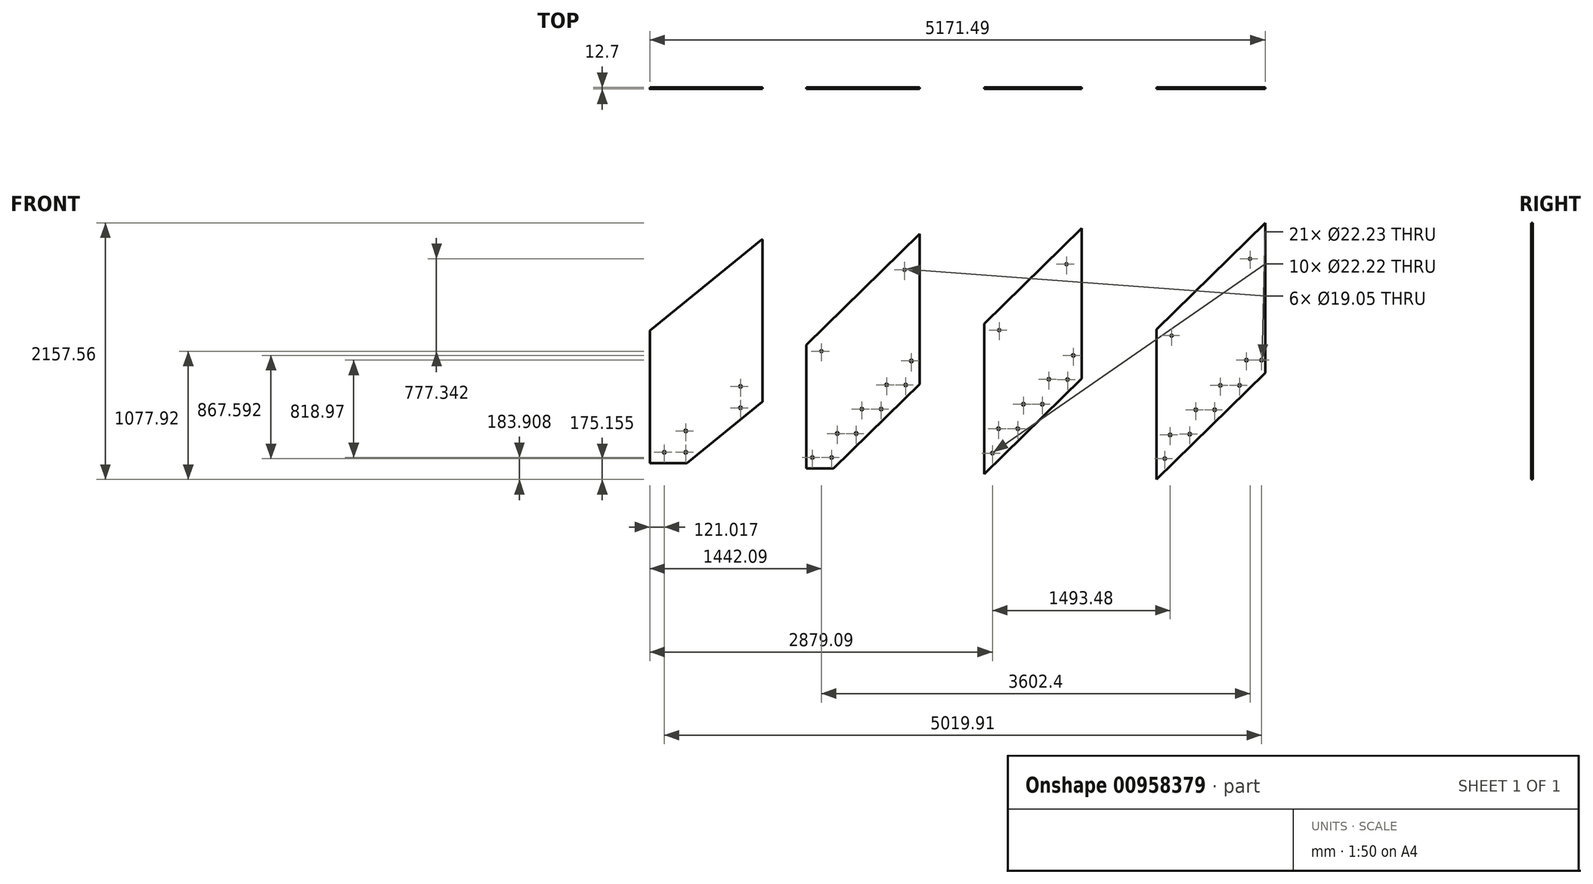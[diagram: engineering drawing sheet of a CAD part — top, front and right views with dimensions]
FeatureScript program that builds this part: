
annotation { "Feature Type Name" : "Feature", "Feature Type Description" : "" }
export const myFeature = defineFeature(function(context is Context, id is Id, definition is map)
    precondition{}
    {
        {
            var Q0;
            Q0=qCreatedBy(makeId("Front.planeOp"),FACE);
            var sketch = newSketch(context, id + "F0", { "sketchPlane" : qUnion([Q0])});
            skLineSegment(sketch, "E0", {"start": v(473.07, -425.21) * mm, "end": v(473.07, 941.15) * mm});
            skLineSegment(sketch, "E1", {"start": v(-161.93, -941.15) * mm, "end": v(-473.08, -941.15) * mm});
            skLineSegment(sketch, "E2", {"start": v(-161.93, -941.15) * mm, "end": v(473.08, -425.21) * mm});
            skLineSegment(sketch, "E3", {"start": v(-473.08, -941.15) * mm, "end": v(-473.08, 172.4) * mm});
            skLineSegment(sketch, "E4", {"start": v(-473.08, 172.4) * mm, "end": v(473.08, 941.15) * mm});
            skCircle(sketch, "E5", {"center": v(-171.45, -670.7) * mm, "radius": 11.11 * mm});
            skCircle(sketch, "E6", {"center": v(-171.45, -850.7) * mm, "radius": 11.11 * mm});
            skCircle(sketch, "E7", {"center": v(288.93, -296.65) * mm, "radius": 11.11 * mm});
            skCircle(sketch, "E8", {"center": v(288.93, -476.65) * mm, "radius": 11.11 * mm});
            skCircle(sketch, "E9", {"center": v(-352.06, -850.7) * mm, "radius": 11.11 * mm});
            skSolve(sketch);
        }
        {
            var Q0;
            Q0=makeQuery(id+"F0.imprint","IMPRINT",FACE,{"disambiguationData":[TD([[makeQuery(id+"F0.imprint","IMPRINT",EDGE,{"derivedFrom":sQuery(id+"F0.wireOp",EDGE,"E0")}),1.0]])]});
            extrude(context, id + "F1", {"entities" : qUnion([Q0]), "depth" : 12.7 * mm, "offsetDistance" : 25.4 * mm});
        }
        {
            var Q0;
            Q0=makeQuery(id+"F1.opExtrude","SWEPT_EDGE",EDGE,{"disambiguationData":[OSD([sQuery(id+"F0.wireOp",EDGE,"E0"),sQuery(id+"F0.wireOp",EDGE,"E4")])]});
            var Q1;
            Q1=makeQuery(id+"F1.opExtrude","SWEPT_EDGE",EDGE,{"disambiguationData":[OSD([sQuery(id+"F0.wireOp",EDGE,"E3"),sQuery(id+"F0.wireOp",EDGE,"E4")])]});
            var Q2;
            Q2=makeQuery(id+"F1.opExtrude","SWEPT_EDGE",EDGE,{"disambiguationData":[OSD([sQuery(id+"F0.wireOp",EDGE,"E1"),sQuery(id+"F0.wireOp",EDGE,"E3")])]});
            var Q3;
            Q3=makeQuery(id+"F1.opExtrude","SWEPT_EDGE",EDGE,{"disambiguationData":[OSD([sQuery(id+"F0.wireOp",EDGE,"E1"),sQuery(id+"F0.wireOp",EDGE,"E2")])]});
            var Q4;
            Q4=makeQuery(id+"F1.opExtrude","SWEPT_EDGE",EDGE,{"disambiguationData":[OSD([sQuery(id+"F0.wireOp",EDGE,"E0"),sQuery(id+"F0.wireOp",EDGE,"E2")])]});
            fillet(context, id + "F2", {"entities" : qUnion([Q0, Q1, Q2, Q3, Q4]), "radius" : 3.17 * mm, "tangentPropagation" : true, "allowEdgeOverflow" : false});
        }
        {
            var Q0;
            Q0=qCreatedBy(makeId("Front.planeOp"),FACE);
            var sketch = newSketch(context, id + "F3", { "sketchPlane" : qUnion([Q0])});
            skLineSegment(sketch, "E10", {"start": v(1661.16, -407.23) * mm, "end": v(1070.61, -986) * mm});
            skLineSegment(sketch, "E11", {"start": v(1794.51, 986) * mm, "end": v(842.01, 52.5) * mm});
            skLineSegment(sketch, "E12", {"start": v(842.01, -986) * mm, "end": v(842.01, 52.5) * mm});
            skCircle(sketch, "E13", {"center": v(892.81, -894.87) * mm, "radius": 11.11 * mm});
            skCircle(sketch, "E14", {"center": v(1054.74, -894.87) * mm, "radius": 11.11 * mm});
            skCircle(sketch, "E15", {"center": v(1261.11, -692.61) * mm, "radius": 11.11 * mm});
            skCircle(sketch, "E16", {"center": v(1470.82, -487.08) * mm, "radius": 11.11 * mm});
            skCircle(sketch, "E17", {"center": v(1308.74, -487.08) * mm, "radius": 11.11 * mm});
            skCircle(sketch, "E18", {"center": v(1516.74, -283.37) * mm, "radius": 11.11 * mm});
            skCircle(sketch, "E19", {"center": v(969.01, -0.86) * mm, "radius": 9.53 * mm});
            skLineSegment(sketch, "E20", {"start": v(1794.51, 986) * mm, "end": v(1794.51, -276.54) * mm});
            skCircle(sketch, "E21", {"center": v(1667.51, 683.72) * mm, "radius": 9.53 * mm});
            skCircle(sketch, "E22", {"center": v(1677.04, -284.98) * mm, "radius": 11.11 * mm});
            skLineSegment(sketch, "E23", {"start": v(1794.51, -276.54) * mm, "end": v(1070.61, -986) * mm});
            skCircle(sketch, "E24", {"center": v(1724.66, -82.7) * mm, "radius": 11.11 * mm});
            skCircle(sketch, "E25", {"center": v(1102.35, -692.61) * mm, "radius": 11.11 * mm});
            skLineSegment(sketch, "E26", {"start": v(842.01, -986) * mm, "end": v(1070.61, -986) * mm});
            skSolve(sketch);
        }
        {
            var Q0;
            Q0=makeQuery(id+"F3.imprint","IMPRINT",FACE,{"disambiguationData":[TD([[makeQuery(id+"F3.imprint","IMPRINT",EDGE,{"derivedFrom":sQuery(id+"F3.wireOp",EDGE,"E11")}),1.0]])]});
            extrude(context, id + "F4", {"entities" : qUnion([Q0]), "depth" : 12.7 * mm, "offsetDistance" : 25.4 * mm});
        }
        {
            var Q0;
            Q0=qCreatedBy(makeId("Front.planeOp"),FACE);
            var sketch = newSketch(context, id + "F5", { "sketchPlane" : qUnion([Q0])});
            skLineSegment(sketch, "E27", {"start": v(3155.31, -229.87) * mm, "end": v(2336.16, -1032.68) * mm});
            skLineSegment(sketch, "E28", {"start": v(3155.31, 1032.68) * mm, "end": v(2336.16, 229.87) * mm});
            skLineSegment(sketch, "E29", {"start": v(2336.16, -1032.68) * mm, "end": v(2336.16, 229.87) * mm});
            skCircle(sketch, "E30", {"center": v(2406.01, -857.53) * mm, "radius": 11.11 * mm});
            skCircle(sketch, "E31", {"center": v(2456.8, -652.16) * mm, "radius": 11.11 * mm});
            skCircle(sketch, "E32", {"center": v(2618.74, -652.16) * mm, "radius": 11.11 * mm});
            skCircle(sketch, "E33", {"center": v(2666.36, -446.78) * mm, "radius": 11.11 * mm});
            skCircle(sketch, "E34", {"center": v(2880.84, -236.58) * mm, "radius": 11.11 * mm});
            skCircle(sketch, "E35", {"center": v(2825.11, -446.79) * mm, "radius": 11.11 * mm});
            skCircle(sketch, "E36", {"center": v(3037.64, -238.5) * mm, "radius": 11.11 * mm});
            skCircle(sketch, "E37", {"center": v(2463.16, 176.5) * mm, "radius": 9.53 * mm});
            skLineSegment(sketch, "E38", {"start": v(3155.31, 1032.68) * mm, "end": v(3155.31, -229.87) * mm});
            skCircle(sketch, "E39", {"center": v(3028.31, 730.4) * mm, "radius": 9.53 * mm});
            skCircle(sketch, "E40", {"center": v(3085.46, -36.03) * mm, "radius": 11.11 * mm});
            skSolve(sketch);
        }
        {
            var Q0;
            Q0=makeQuery(id+"F5.imprint","IMPRINT",FACE,{"disambiguationData":[TD([[makeQuery(id+"F5.imprint","IMPRINT",EDGE,{"derivedFrom":sQuery(id+"F5.wireOp",EDGE,"E28")}),1.0]])]});
            extrude(context, id + "F6", {"entities" : qUnion([Q0]), "depth" : 12.7 * mm, "offsetDistance" : 25.4 * mm});
        }
        {
            var Q0;
            Q0=qCreatedBy(makeId("Front.planeOp"),FACE);
            var sketch = newSketch(context, id + "F7", { "sketchPlane" : qUnion([Q0])});
            skLineSegment(sketch, "E41", {"start": v(4698.4, -183.77) * mm, "end": v(3785.2, -1078.78) * mm});
            skLineSegment(sketch, "E42", {"start": v(4698.4, 1078.78) * mm, "end": v(3785.2, 183.77) * mm});
            skLineSegment(sketch, "E43", {"start": v(3785.2, -1078.78) * mm, "end": v(3785.2, 183.77) * mm});
            skCircle(sketch, "E44", {"center": v(3855.04, -903.62) * mm, "radius": 11.11 * mm});
            skCircle(sketch, "E45", {"center": v(3899.5, -704.47) * mm, "radius": 11.11 * mm});
            skCircle(sketch, "E46", {"center": v(4064.6, -698.25) * mm, "radius": 11.11 * mm});
            skCircle(sketch, "E47", {"center": v(4115.4, -492.87) * mm, "radius": 11.11 * mm});
            skCircle(sketch, "E48", {"center": v(4321.77, -288.16) * mm, "radius": 11.11 * mm});
            skCircle(sketch, "E49", {"center": v(4540.84, -75.9) * mm, "radius": 11.11 * mm});
            skCircle(sketch, "E50", {"center": v(4274.14, -492.88) * mm, "radius": 11.11 * mm});
            skCircle(sketch, "E51", {"center": v(4483.03, -288.16) * mm, "radius": 11.11 * mm});
            skCircle(sketch, "E52", {"center": v(3912.2, 130.42) * mm, "radius": 9.53 * mm});
            skCircle(sketch, "E53", {"center": v(4667.84, -75.9) * mm, "radius": 11.11 * mm});
            skLineSegment(sketch, "E54", {"start": v(4698.4, 1078.78) * mm, "end": v(4698.4, -183.77) * mm});
            skCircle(sketch, "E55", {"center": v(4571.4, 776.48) * mm, "radius": 9.53 * mm});
            skSolve(sketch);
        }
        {
            var Q0;
            Q0=makeQuery(id+"F7.imprint","IMPRINT",FACE,{"disambiguationData":[TD([[makeQuery(id+"F7.imprint","IMPRINT",EDGE,{"derivedFrom":sQuery(id+"F7.wireOp",EDGE,"E41")}),-1.0]])]});
            extrude(context, id + "F8", {"entities" : qUnion([Q0]), "depth" : 12.7 * mm, "offsetDistance" : 25.4 * mm});
        }
    });
